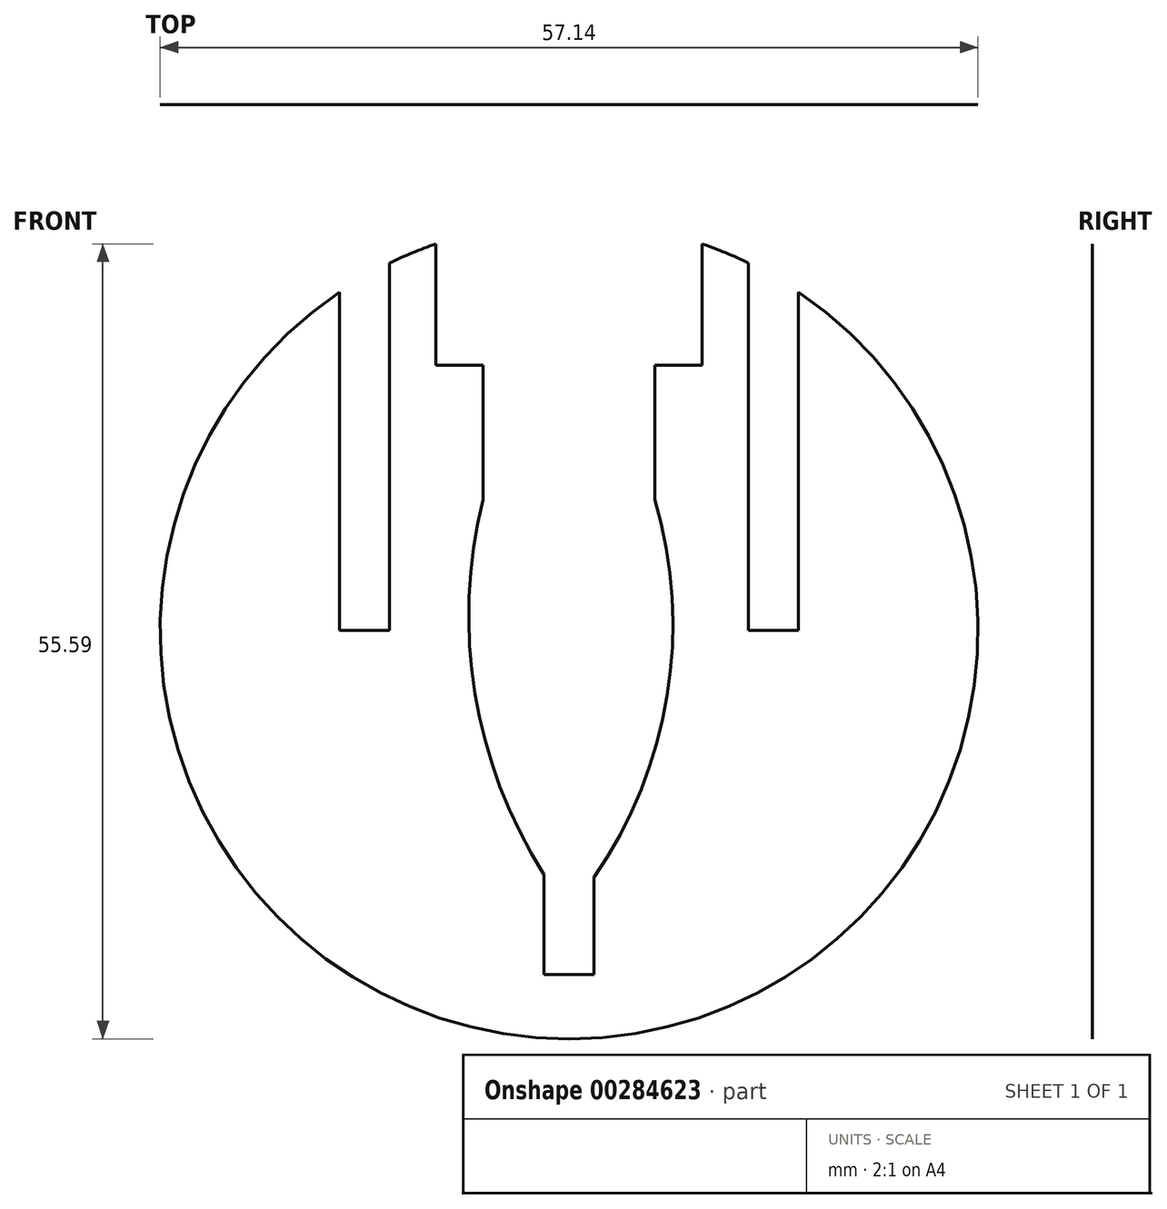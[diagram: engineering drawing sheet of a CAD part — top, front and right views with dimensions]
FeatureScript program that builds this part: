
annotation { "Feature Type Name" : "Feature", "Feature Type Description" : "" }
export const myFeature = defineFeature(function(context is Context, id is Id, definition is map)
    precondition{}
    {
        {
            var Q0;
            Q0=qCreatedBy(makeId("Front.planeOp"),FACE);
            var sketch = newSketch(context, id + "F0", { "sketchPlane" : qUnion([Q0])});
            skCircle(sketch, "E0", {"center": v(0, 0) * mm, "radius": 28.58 * mm});
            skSolve(sketch);
        }
        {
            var Q0;
            Q0=qSketchRegion(id+"F0",true);
            extrude(context, id + "F1", {"entities" : qUnion([Q0]), "depth" : 1 / 203.2 * mm});
        }
        {
            var Q0;
            Q0=makeQuery(id+"F1.opExtrude","CAP_FACE",FACE,{"disambiguationData":[OSD([sQuery(id+"F0.wireOp",EDGE,"E0")])],"isStart":false});
            var sketch = newSketch(context, id + "F2", { "sketchPlane" : qUnion([Q0])});
            skLineSegment(sketch, "E1", {"start": v(-1.75, -24.08) * mm, "end": v(1.75, -24.08) * mm});
            skLineSegment(sketch, "E2", {"start": v(-16.04, 0) * mm, "end": v(-12.54, 0) * mm});
            skLineSegment(sketch, "E3", {"start": v(12.54, 0) * mm, "end": v(16.04, 0) * mm});
            skLineSegment(sketch, "E4", {"start": v(0, 0) * mm, "end": v(0, -28.58) * mm});
            skPoint(sketch, "E5", {"position": v(0, -24.08) * mm});
            skLineSegment(sketch, "E6", {"start": v(0, 0) * mm, "end": v(-28.58, 0) * mm});
            skPoint(sketch, "E7", {"position": v(-14.29, 0) * mm});
            skLineSegment(sketch, "E8", {"start": v(0, 0) * mm, "end": v(28.58, 0) * mm});
            skPoint(sketch, "E9", {"position": v(14.29, 0) * mm});
            skLineSegment(sketch, "E10", {"start": v(-9.3, 27.02) * mm, "end": v(-9.3, 18.52) * mm});
            skLineSegment(sketch, "E11", {"start": v(-9.3, 18.52) * mm, "end": v(-6, 18.52) * mm});
            skLineSegment(sketch, "E12", {"start": v(-6, 18.52) * mm, "end": v(-6, 9.13) * mm});
            skLineSegment(sketch, "E13", {"start": v(6, 9.13) * mm, "end": v(6, 18.52) * mm});
            skLineSegment(sketch, "E14", {"start": v(6, 18.52) * mm, "end": v(9.3, 18.52) * mm});
            skLineSegment(sketch, "E15", {"start": v(9.3, 18.52) * mm, "end": v(9.3, 27.02) * mm});
            skArc(sketch, "E16", {"start": v(-6, 9.13) * mm, "mid": v(-6.3, -5.91) * mm, "end": v(0, -19.58) * mm});
            skArc(sketch, "E17", {"start": v(0, -19.58) * mm, "mid": v(6.6, -5.97) * mm, "end": v(6, 9.13) * mm});
            skLineSegment(sketch, "E18", {"start": v(-16.04, 0) * mm, "end": v(-16.04, 23.65) * mm});
            skLineSegment(sketch, "E19", {"start": v(-12.54, 0) * mm, "end": v(-12.54, 25.68) * mm});
            skLineSegment(sketch, "E20", {"start": v(12.54, 0) * mm, "end": v(12.54, 25.68) * mm});
            skLineSegment(sketch, "E21", {"start": v(16.04, 0) * mm, "end": v(16.04, 23.65) * mm});
            skLineSegment(sketch, "E22", {"start": v(1.75, -24.08) * mm, "end": v(1.75, -17.28) * mm});
            skLineSegment(sketch, "E23", {"start": v(-1.75, -24.08) * mm, "end": v(-1.75, -17.08) * mm});
            skSolve(sketch);
        }
        {
            var Q0;
            {var subQ0=sQuery(id+"F2.wireOp",EDGE,"E23");Q0=makeQuery(id+"F2.imprint","IMPRINT",FACE,{"disambiguationData":[TD([[makeQuery(id+"F2.imprint","IMPRINT",EDGE,{"derivedFrom":subQ0}),-1.0]])]});}
            var Q1;
            {var subQ0=sQuery(id+"F2.wireOp",EDGE,"E22");Q1=makeQuery(id+"F2.imprint","IMPRINT",FACE,{"disambiguationData":[TD([[makeQuery(id+"F2.imprint","IMPRINT",EDGE,{"derivedFrom":subQ0}),1.0]])]});}
            var Q2;
            {var subQ3=sQuery(id+"F2.wireOp",EDGE,"E16");var subQ6=makeQuery(id+"F2.imprint","INTERSECT",VERTEX,{"derivedFrom":[subQ3,sQuery(id+"F2.wireOp",EDGE,"E23")]});Q2=makeQuery(id+"F2.imprint","IMPRINT",FACE,{"disambiguationData":[TD([[makeQuery(id+"F2.imprint","IMPRINT",EDGE,{"disambiguationData":[TD([[subQ6,1.0]])],"derivedFrom":subQ3}),1.0]])]});}
            var Q3;
            {var subQ3=sQuery(id+"F2.wireOp",EDGE,"E17");var subQ5=makeQuery(id+"F2.imprint","INTERSECT",VERTEX,{"derivedFrom":[subQ3,sQuery(id+"F2.wireOp",EDGE,"E22")]});Q3=makeQuery(id+"F2.imprint","IMPRINT",FACE,{"disambiguationData":[TD([[makeQuery(id+"F2.imprint","IMPRINT",EDGE,{"disambiguationData":[TD([[subQ5,-1.0]])],"derivedFrom":subQ3}),1.0]])]});}
            var Q4;
            {var subQ10=sQuery(id+"F2.wireOp",EDGE,"E10");Q4=makeQuery(id+"F2.imprint","IMPRINT",FACE,{"disambiguationData":[TD([[makeQuery(id+"F2.imprint","IMPRINT",EDGE,{"derivedFrom":subQ10}),1.0]])]});}
            var Q5;
            {var subQ0=sQuery(id+"F2.wireOp",EDGE,"E20");Q5=makeQuery(id+"F2.imprint","IMPRINT",FACE,{"disambiguationData":[TD([[makeQuery(id+"F2.imprint","IMPRINT",EDGE,{"derivedFrom":subQ0}),-1.0]])]});}
            var Q6;
            {var subQ0=sQuery(id+"F2.wireOp",EDGE,"E18");Q6=makeQuery(id+"F2.imprint","IMPRINT",FACE,{"disambiguationData":[TD([[makeQuery(id+"F2.imprint","IMPRINT",EDGE,{"derivedFrom":subQ0}),-1.0]])]});}
            extrude(context, id + "F3", {"entities" : qUnion([Q0, Q1, Q2, Q3, Q4, Q5, Q6]), "operationType" : NewBodyOperationType.REMOVE, "endBound" : BoundingType.THROUGH_ALL, "oppositeDirection" : true, "depth" : 25 * mm});
        }
    });
